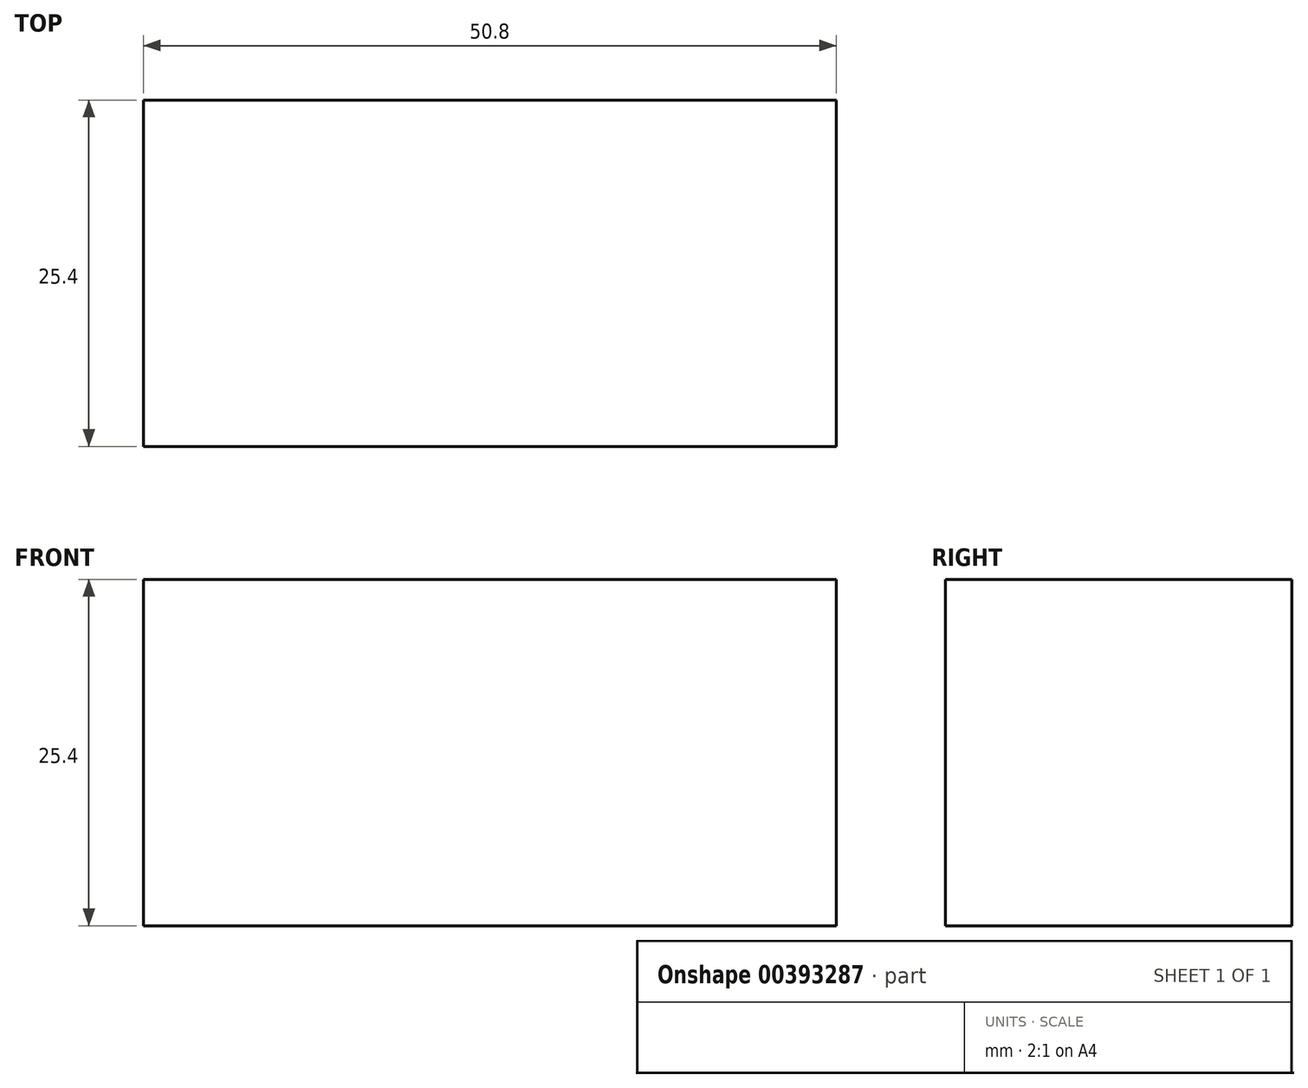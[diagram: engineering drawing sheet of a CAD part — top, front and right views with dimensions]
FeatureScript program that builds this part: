
annotation { "Feature Type Name" : "Feature", "Feature Type Description" : "" }
export const myFeature = defineFeature(function(context is Context, id is Id, definition is map)
    precondition{}
    {
        {
            var Q0;
            Q0=qCreatedBy(makeId("Front.planeOp"),FACE);
            var sketch = newSketch(context, id + "F0", { "sketchPlane" : qUnion([Q0])});
            skLineSegment(sketch, "E0.bottom", {"start": v(-25.4, -12.7) * mm, "end": v(25.4, -12.7) * mm});
            skLineSegment(sketch, "E0.top", {"start": v(-25.4, 12.7) * mm, "end": v(25.4, 12.7) * mm});
            skLineSegment(sketch, "E0.left", {"start": v(-25.4, -12.7) * mm, "end": v(-25.4, 12.7) * mm});
            skLineSegment(sketch, "E0.right", {"start": v(25.4, -12.7) * mm, "end": v(25.4, 12.7) * mm});
            skPoint(sketch, "E0.middle", {"position": v(0, 0) * mm});
            skSolve(sketch);
        }
        {
            var Q0;
            Q0=makeQuery(id+"F0.imprint","IMPRINT",FACE,{"disambiguationData":[TD([[makeQuery(id+"F0.imprint","IMPRINT",EDGE,{"derivedFrom":sQuery(id+"F0.wireOp",EDGE,"E0.bottom")}),1.0]])]});
            extrude(context, id + "F1", {"entities" : qUnion([Q0]), "depth" : 25.4 * mm});
        }
    });
